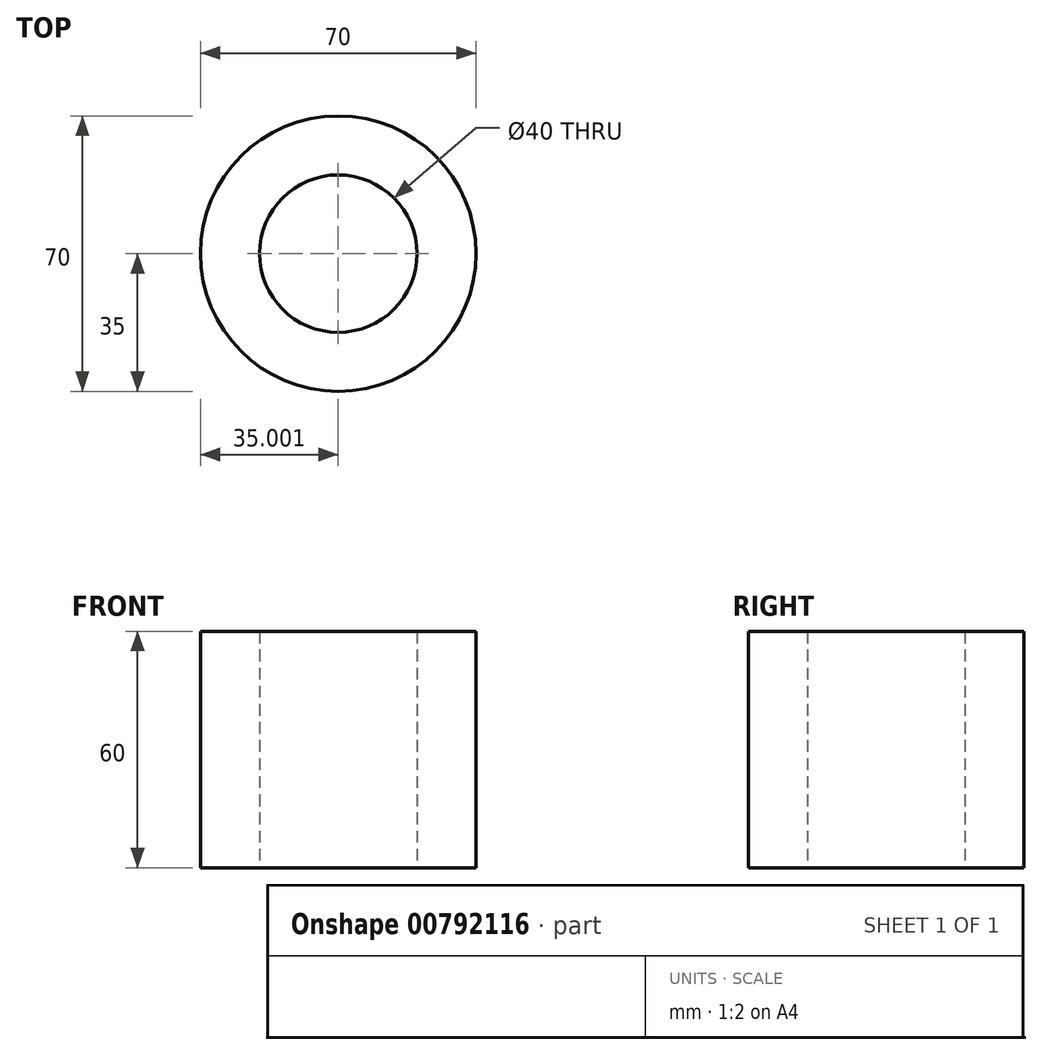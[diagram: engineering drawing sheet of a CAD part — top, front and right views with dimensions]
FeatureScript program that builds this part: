
annotation { "Feature Type Name" : "Feature", "Feature Type Description" : "" }
export const myFeature = defineFeature(function(context is Context, id is Id, definition is map)
    precondition{}
    {
        {
            var Q0;
            Q0=qCreatedBy(makeId("Top.planeOp"),FACE);
            var sketch = newSketch(context, id + "F0", { "sketchPlane" : qUnion([Q0])});
            skCircle(sketch, "E0", {"center": v(-84.7, -21.66) * mm, "radius": 35 * mm});
            skCircle(sketch, "E1", {"center": v(-84.7, -21.66) * mm, "radius": 20 * mm});
            skCircle(sketch, "E2", {"center": v(15.3, 28.34) * mm, "radius": 10 * mm});
            skCircle(sketch, "E3", {"center": v(15.3, 28.34) * mm, "radius": 25 * mm});
            skCircle(sketch, "E4.MirrorC", {"center": v(15.3, -71.66) * mm, "radius": 25 * mm});
            skCircle(sketch, "E5.MirrorC", {"center": v(15.3, -71.66) * mm, "radius": 10 * mm});
            skLineSegment(sketch, "E6", {"start": v(-97.49, 10.92) * mm, "end": v(6.16, 51.61) * mm});
            skLineSegment(sketch, "E7", {"start": v(40.3, 28.34) * mm, "end": v(40.3, -71.66) * mm});
            skLineSegment(sketch, "E8", {"start": v(-97.49, -54.24) * mm, "end": v(6.16, -94.93) * mm});
            skPoint(sketch, "E9.orphan", {"position": v(15.3, -21.66) * mm});
            skSolve(sketch);
        }
        {
            var Q0;
            Q0=makeQuery(id+"F0.imprint","IMPRINT",FACE,{"disambiguationData":[TD([[makeQuery(id+"F0.imprint","IMPRINT",EDGE,{"derivedFrom":sQuery(id+"F0.wireOp",EDGE,"E1")}),-1.0]])]});
            extrude(context, id + "F1", {"entities" : qUnion([Q0]), "depth" : 60 * mm, "offsetDistance" : 25 * mm});
        }
    });
